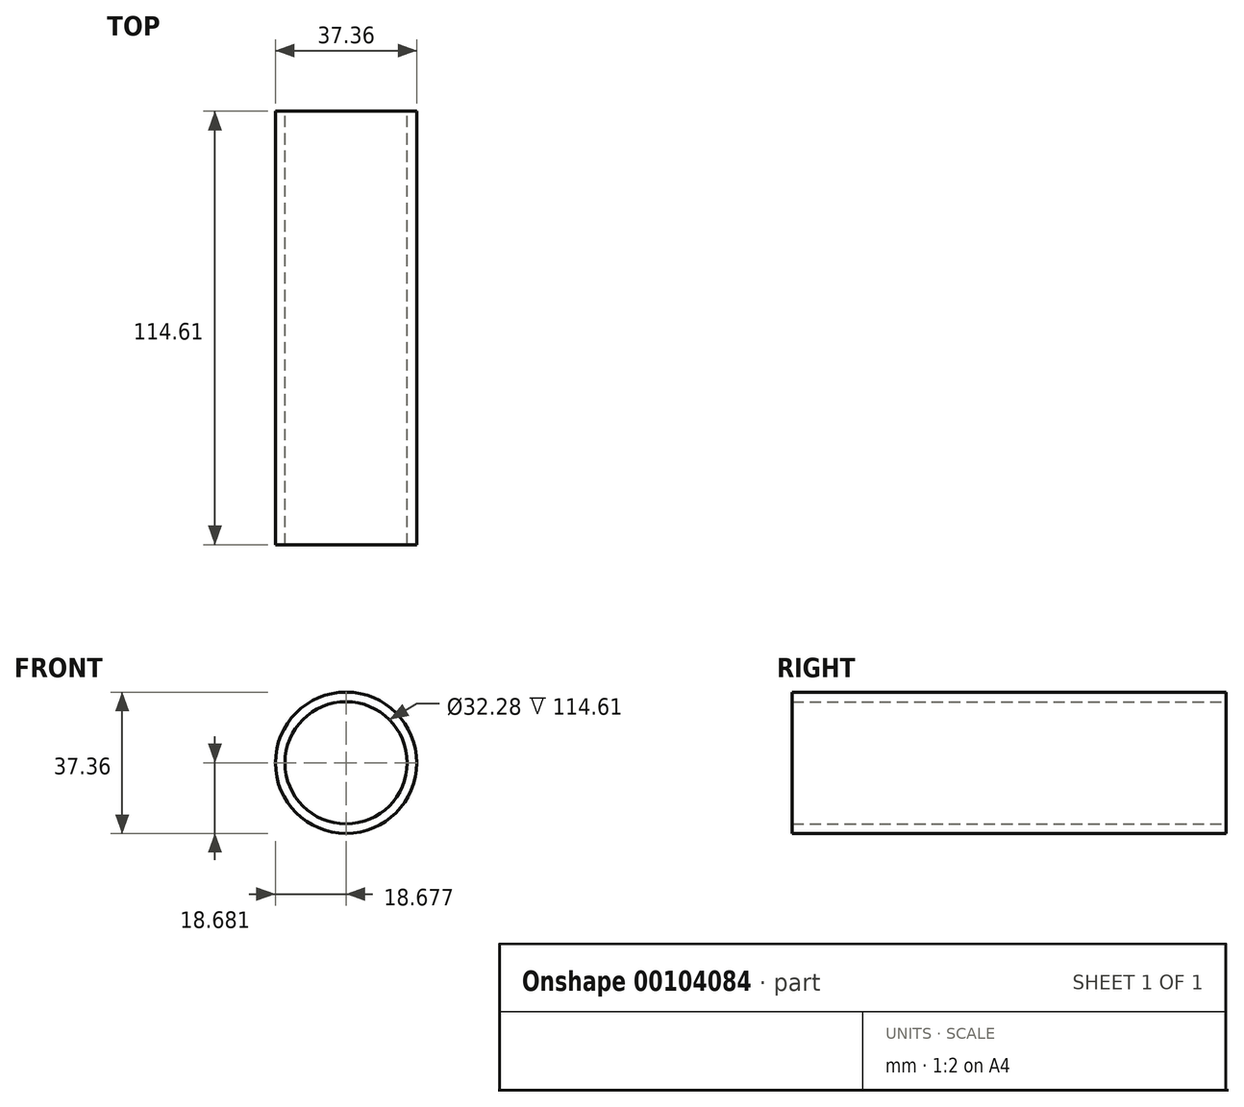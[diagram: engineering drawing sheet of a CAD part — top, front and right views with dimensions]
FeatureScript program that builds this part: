
annotation { "Feature Type Name" : "Feature", "Feature Type Description" : "" }
export const myFeature = defineFeature(function(context is Context, id is Id, definition is map)
    precondition{}
    {
        {
            var Q0;
            Q0=qCreatedBy(makeId("Front.planeOp"),FACE);
            var sketch = newSketch(context, id + "F0", { "sketchPlane" : qUnion([Q0])});
            skCircle(sketch, "E0", {"center": v(2.96, 5.85) * mm, "radius": 18.68 * mm});
            skSolve(sketch);
        }
        {
            var Q0;
            Q0 = qSketchRegion(id + "F0", true);
            extrude(context, id + "F1", {"entities" : qUnion([Q0]), "depth" : 114.61 * mm});
        }
        {
            var Q0;
            Q0=makeQuery(id+"F1.opExtrude","CAP_FACE",FACE,{"disambiguationData":[OSD([sQuery(id+"F0.wireOp",EDGE,"E0")])],"isStart":false});
            var Q1;
            Q1=makeQuery(id+"F1.opExtrude","CAP_FACE",FACE,{"disambiguationData":[OSD([sQuery(id+"F0.wireOp",EDGE,"E0")])],"isStart":true});
            shell(context, id + "F2", {"entities" : qUnion([Q0, Q1]), "thickness" : 2.54 * mm});
        }
    });
